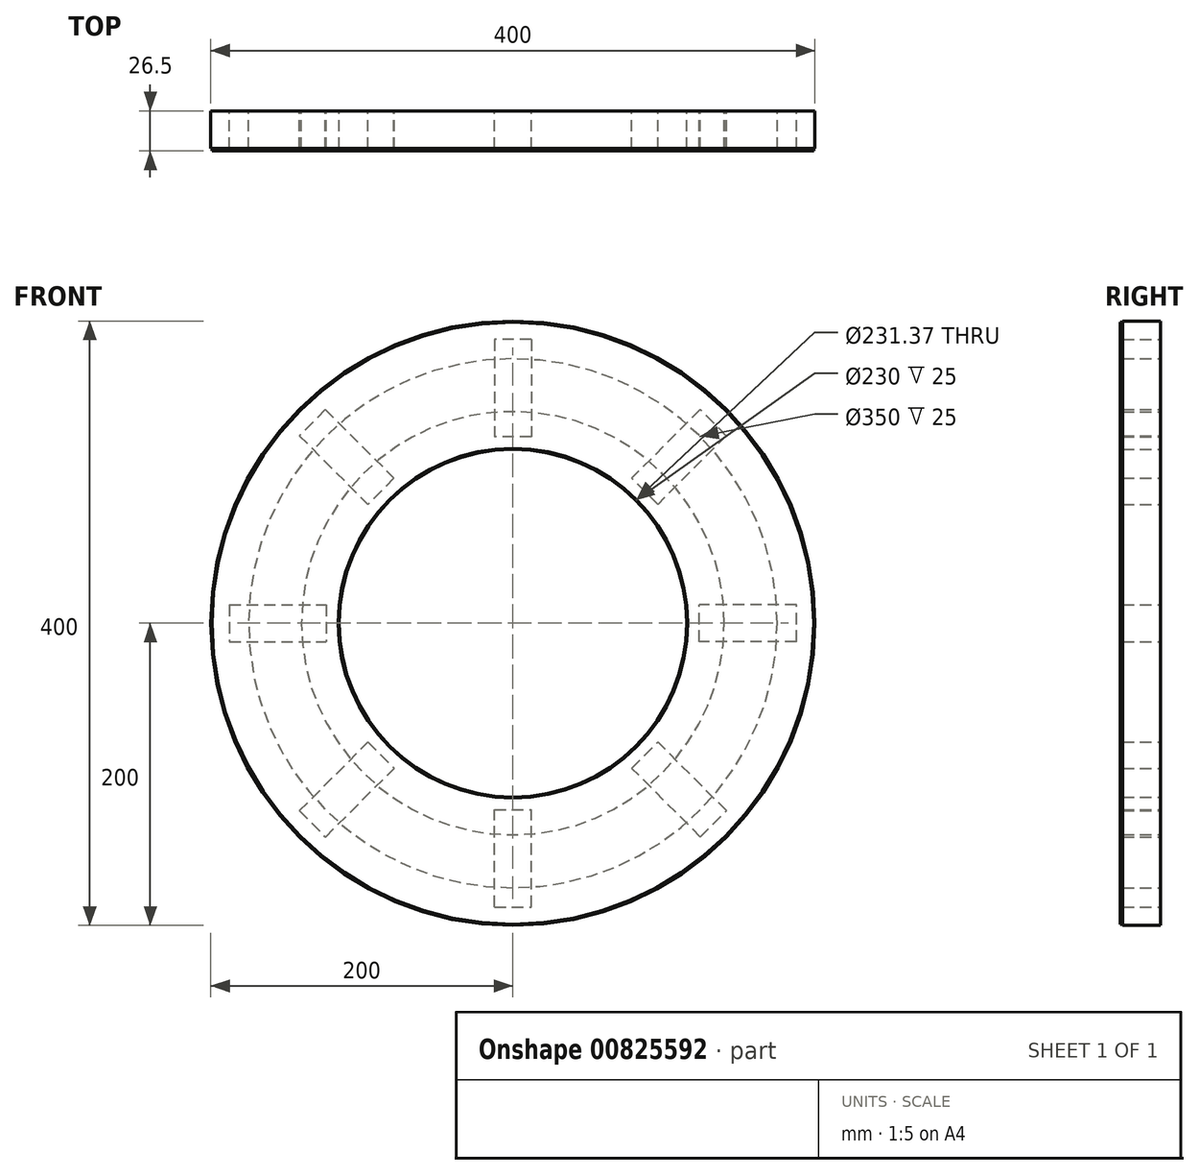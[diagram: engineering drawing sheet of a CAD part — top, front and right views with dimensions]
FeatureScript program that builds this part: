
annotation { "Feature Type Name" : "Feature", "Feature Type Description" : "" }
export const myFeature = defineFeature(function(context is Context, id is Id, definition is map)
    precondition{}
    {
        {
            var Q0;
            Q0=qCreatedBy(makeId("Front.planeOp"),FACE);
            var sketch = newSketch(context, id + "F0", { "sketchPlane" : qUnion([Q0])});
            skCircle(sketch, "E0", {"center": v(0, 0) * mm, "radius": 115 * mm});
            skCircle(sketch, "E1.0", {"center": v(0, 0) * mm, "radius": 140 * mm});
            skCircle(sketch, "E2", {"center": v(0, 0) * mm, "radius": 200 * mm});
            skCircle(sketch, "E3.0", {"center": v(0, 0) * mm, "radius": 175 * mm});
            skSolve(sketch);
        }
        {
            var Q0;
            Q0=makeQuery(id+"F0.imprint","IMPRINT",FACE,{"disambiguationData":[TD([[makeQuery(id+"F0.imprint","IMPRINT",EDGE,{"derivedFrom":sQuery(id+"F0.wireOp",EDGE,"E0")}),-1.0]])]});
            var Q1;
            Q1=makeQuery(id+"F0.imprint","IMPRINT",FACE,{"disambiguationData":[TD([[makeQuery(id+"F0.imprint","IMPRINT",EDGE,{"derivedFrom":sQuery(id+"F0.wireOp",EDGE,"E2")}),1.0]])]});
            extrude(context, id + "F1", {"entities" : qUnion([Q0, Q1]), "depth" : 25 * mm, "offsetDistance" : 25 * mm});
        }
        {
            var Q0;
            Q0=makeQuery(id+"F1.opExtrude","CAP_FACE",FACE,{"disambiguationData":[OSD([sQuery(id+"F0.wireOp",EDGE,"E0"),sQuery(id+"F0.wireOp",EDGE,"E1.0")])],"isStart":false});
            var sketch = newSketch(context, id + "F2", { "sketchPlane" : qUnion([Q0])});
            skCircle(sketch, "E4", {"center": v(0, 0) * mm, "radius": 115.69 * mm});
            skCircle(sketch, "E5", {"center": v(0, 0) * mm, "radius": 199.11 * mm});
            skSolve(sketch);
        }
        {
            var Q0;
            Q0=makeQuery(id+"F2.imprint","IMPRINT",FACE,{"disambiguationData":[TD([[makeQuery(id+"F2.imprint","IMPRINT",EDGE,{"derivedFrom":sQuery(id+"F2.wireOp",EDGE,"E4")}),-1.0]])]});
            var Q1;
            Q1=makeQuery(id+"F2.imprint","IMPRINT",FACE,{"disambiguationData":[TD([[makeQuery(id+"F2.imprint","IMPRINT",EDGE,{"derivedFrom":sQuery(id+"F2.wireOp",EDGE,"E5")}),1.0]])]});
            extrude(context, id + "F3", {"entities" : qUnion([Q0, Q1]), "depth" : 1.5 * mm, "offsetDistance" : 25 * mm});
        }
        {
            var Q0;
            Q0=makeQuery(id+"F1.opExtrude","CAP_FACE",FACE,{"disambiguationData":[OSD([sQuery(id+"F0.wireOp",EDGE,"E0"),sQuery(id+"F0.wireOp",EDGE,"E1.0")])],"isStart":true});
            var sketch = newSketch(context, id + "F4", { "sketchPlane" : qUnion([Q0])});
            skLineSegment(sketch, "E6", {"start": v(0, 259.7) * mm, "end": v(0, -249.72) * mm, "construction": true});
            skLineSegment(sketch, "E7.0", {"start": v(-12.5, 187.54) * mm, "end": v(-12.5, -249.72) * mm, "construction": true});
            skLineSegment(sketch, "E8.0", {"start": v(12.5, 187.54) * mm, "end": v(12.5, -249.72) * mm, "construction": true});
            skLineSegment(sketch, "E9.bottom", {"start": v(-12.5, 187.54) * mm, "end": v(12.5, 187.54) * mm});
            skLineSegment(sketch, "E9.top", {"start": v(-12.5, 123.36) * mm, "end": v(12.5, 123.36) * mm});
            skLineSegment(sketch, "E9.left", {"start": v(-12.5, 187.54) * mm, "end": v(-12.5, 123.36) * mm});
            skLineSegment(sketch, "E9.right", {"start": v(12.5, 187.54) * mm, "end": v(12.5, 123.36) * mm});
            skSolve(sketch);
        }
        {
            var Q0;
            {var subQ1=sQuery(id+"F4.wireOp",EDGE,"E9.top");Q0=makeQuery(id+"F4.imprint","IMPRINT",FACE,{"disambiguationData":[TD([[makeQuery(id+"F4.imprint","IMPRINT",EDGE,{"derivedFrom":subQ1}),-1.0]])]});}
            var sketch = newSketch(context, id + "F5", { "sketchPlane" : qUnion([Q0])});
            skLineSegment(sketch, "E10.bottom", {"start": v(-12.16, 187.71) * mm, "end": v(12.27, 187.71) * mm});
            skLineSegment(sketch, "E10.top", {"start": v(-12.16, 123.5) * mm, "end": v(12.27, 123.5) * mm});
            skLineSegment(sketch, "E10.left", {"start": v(-12.16, 187.71) * mm, "end": v(-12.16, 123.5) * mm});
            skLineSegment(sketch, "E10.right", {"start": v(12.27, 187.71) * mm, "end": v(12.27, 123.5) * mm});
            skSolve(sketch);
        }
        {
            var Q0;
            Q0 = qSketchRegion(id + "F5", true);
            extrude(context, id + "F6", {"entities" : qUnion([Q0]), "oppositeDirection" : true, "depth" : 25 * mm, "offsetDistance" : 25 * mm});
        }
        {
            var Q0;
            Q0=qCreatedBy(makeId("Right.planeOp"),FACE);
            var sketch = newSketch(context, id + "F7", { "sketchPlane" : qUnion([Q0])});
            skLineSegment(sketch, "E11", {"start": v(-73.66, 0) * mm, "end": v(70.26, 0) * mm, "construction": true});
            skSolve(sketch);
        }
        {
            var Q0;
            Q0=makeQuery(id+"F6.opExtrude","SWEPT_BODY",BODY,{"disambiguationData":[OSD([sQuery(id+"F5.wireOp",EDGE,"E10.bottom"),sQuery(id+"F5.wireOp",EDGE,"E10.top"),sQuery(id+"F5.wireOp",EDGE,"E10.left"),sQuery(id+"F5.wireOp",EDGE,"E10.right")])]});
            var Q1;
            Q1=sQuery(id+"F7.wireOp",EDGE,"E11");
            circularPattern(context, id + "F8", {"entities" : qUnion([Q0]), "axis" : qUnion([Q1]), "angle" : 360 * degree, "instanceCount" : 8, "equalSpace" : true});
        }
    });
